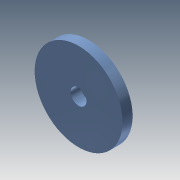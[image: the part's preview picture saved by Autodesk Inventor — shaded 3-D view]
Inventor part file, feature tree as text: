
AUTODESK INVENTOR PART (.ipt)
format: ipt  version: 2015 (Build 190159000, 159)  size: 115,200 bytes
history: native  units: mm
features: extrude x6, sketch x6
ambient origin geometry x8: Origin, YZ Plane, XZ Plane, XY Plane, X Axis, Y Axis, Z Axis, Center Point
bodies: Solid1 (feature_tree)
feature tree (12):
  extrude  "Extrusion1"  Depth=3.8mm TaperAngle=0.0deg
  extrude  "Extrusion2"  Depth=1.0mm TaperAngle=0.0deg
  extrude  "Extrusion3"  Depth=3.8mm TaperAngle=0.0deg
  extrude  "Extrusion4"  Depth=3.6mm TaperAngle=0.0deg
  extrude  "Extrusion5"  Depth=3.6mm TaperAngle=0.0deg
  extrude  "Extrusion6"  Depth=3.8mm TaperAngle=0.0deg
  sketch  "Sketch1"  dims[d0=33.15mm d1=3.8mm d2=0.0mm]
  sketch  "Sketch2"  dims[d3=28.0mm d4=1.0mm d5=0.0mm]
  sketch  "Sketch3"  dims[d6=10.0mm d7=3.8mm d8=0.0mm]
  sketch  "Sketch4"  dims[d9=3.6mm d10=3.6mm d11=0.0mm]
  sketch  "Sketch5"  dims[d12=6.0mm d13=3.6mm d14=0.0mm]
  sketch  "Sketch6"  dims[d15=6.0mm d16=3.8mm d17=0.0mm]
